# Revit family: Faucet-Wall_Mount-Bath_Spout-KOHLER-Aleo-K-99061IN
name_source: partatom
category: Plumbing Fixtures
revit_build: Autodesk Revit 2017 (Build: 20160225_1515(x64)
units: mm (PartAtom-declared; Revit-internal decimal feet)

## family parameters
Cut with Voids When Loaded = No
Host = Face
OmniClass Number = 23.31.11.00
OmniClass Title = Faucets
Part Type = Normal
Room Calculation Point = No
Round Connector Dimension = Use Diameter
Shared = No

## types (2) — shared parameters
ADA Compliant = No
Assembly Code = D2010
CW Connection = No
Cold Water Inlet = Cold Water Inlet
Date Modified = 10/26/2020
Default Elevation = 36"
Description = WALL MOUNT BATH SPOUT WITH OUT DIVERTER
Drain Included = No
Flow Rate = 0 GPM
HW Connection = Yes
Height = 2 3/4"
Hot Water Inlet = Hot Water Inlet
Length = 6 1/4"
Manufacturer = KOHLER Co.
Master Format 2014 = 22 41 39
Master Format 2014 Name = Residential Faucets, Supplies, and Trim
Material = Premium Metal Construction
Pressure = 0.00 psi
Product Documentation Link = http://resources.kohler.com
Product Name = Aleo
Product Page URL = https://www.kohler.co.in
Spout Reach = 6 1/4"
Tempered Water Inlet = Tempered Water Inlet
URL = https://www.kohler.co.in
Vent Connection = No
Waste Connection = No
Waste Water Outlet = Waste Water Outlet
WaterSense Certified = No
Width = 2 3/4"

## per-type parameters (varying)
| type | Finish | Model | Type |
| AF- Vibrant French Gold | Kohler-Metal-AF-Vibrant_French_Gold | K-99061IN-AF | 1 |
| CP-Polished Chrome | Kohler-Metal-CP-Polished_Chrome | K-99061IN-CP | 2 |

## geometry (parser evidence)
native form markers: Sweep x6
no freeform markers — native parametric forms only
